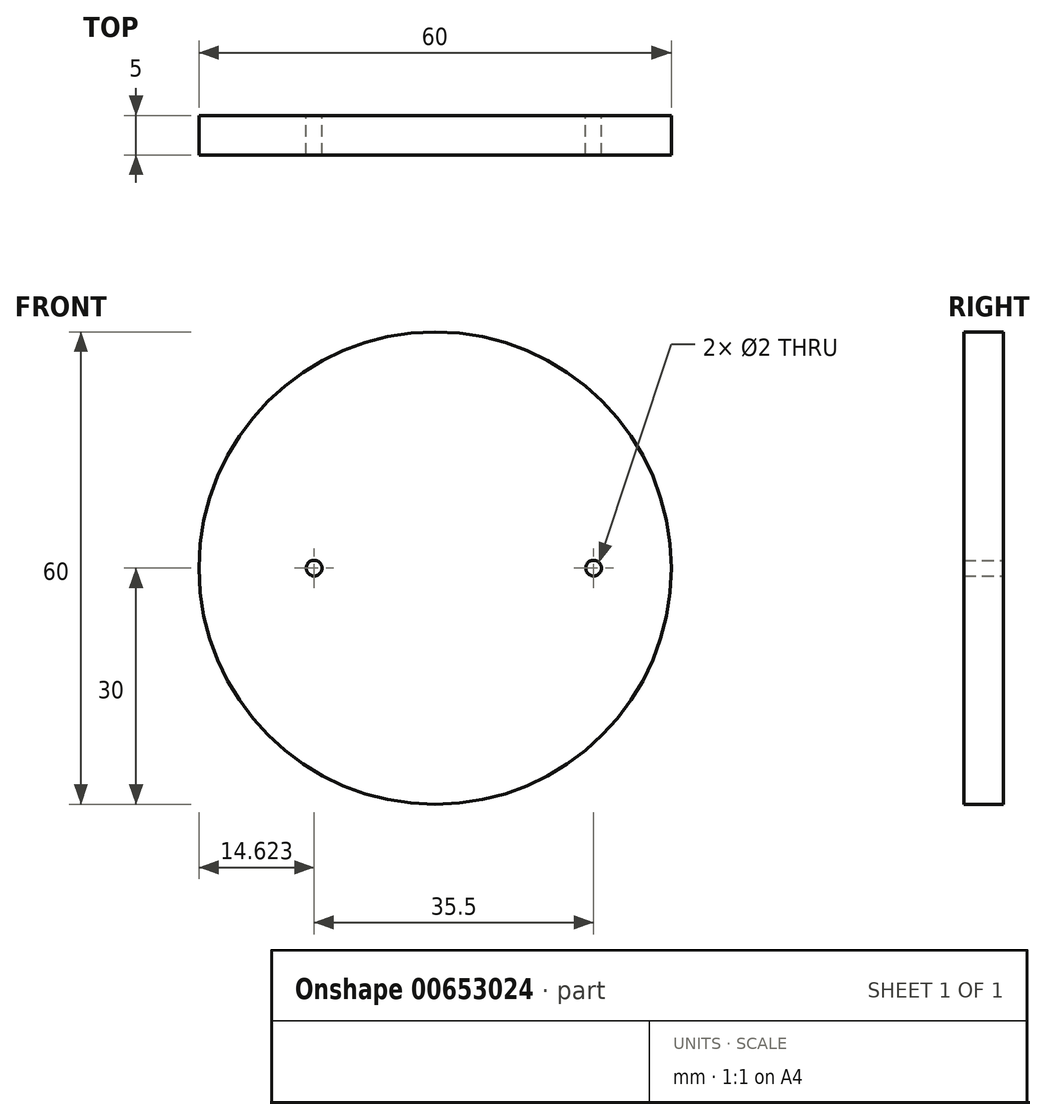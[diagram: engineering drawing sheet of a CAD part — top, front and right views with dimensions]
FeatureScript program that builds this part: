
annotation { "Feature Type Name" : "Feature", "Feature Type Description" : "" }
export const myFeature = defineFeature(function(context is Context, id is Id, definition is map)
    precondition{}
    {
        {
            var Q0;
            Q0=qCreatedBy(makeId("Front.planeOp"),FACE);
            var sketch = newSketch(context, id + "F0", { "sketchPlane" : qUnion([Q0])});
            skCircle(sketch, "E0", {"center": v(0, 0) * mm, "radius": 30 * mm});
            skCircle(sketch, "E1", {"center": v(20.12, 0) * mm, "radius": 1 * mm});
            skCircle(sketch, "E2", {"center": v(-15.38, 0) * mm, "radius": 1 * mm});
            skFitSpline(sketch, "E3", {"points": [v(-13.73, 18.62) * mm, v(-21.55, 16.33) * mm, v(-19.83, 10.31) * mm, v(-26.9, 5.93) * mm, v(-24.89, -0.94) * mm, v(-25.84, -10.2) * mm, v(-21.36, -10.3) * mm, v(-16.97, -17.07) * mm, v(-10.67, -16.78) * mm, v(-8.48, -23.56) * mm, v(1.73, -22.03) * mm, v(6.88, -25.08) * mm, v(8.7, -25.37) * mm, v(17.38, -16.4) * mm, v(19.67, -17.54) * mm, v(20.81, -14.68) * mm, v(21.67, -10.58) * mm, v(26.06, -9.34) * mm, v(23.67, -2.28) * mm, v(26.92, 4.2) * mm, v(23.58, 9.93) * mm, v(22.15, 17.37) * mm, v(11.94, 20.05) * mm, v(9.7, 25.39) * mm, v(2.91, 19.9) * mm, v(-6.8, 23.56) * mm, v(-13.77, 24.29) * mm, v(-13.73, 18.62) * mm]});
            skLineSegment(sketch, "E4", {"start": v(-4.64, -5.3) * mm, "end": v(0, 6.66) * mm});
            skLineSegment(sketch, "E5", {"start": v(0, 6.66) * mm, "end": v(5.35, -5.3) * mm});
            skLineSegment(sketch, "E6", {"start": v(5.35, -5.3) * mm, "end": v(-6.86, 1.85) * mm});
            skLineSegment(sketch, "E7", {"start": v(-6.86, 1.85) * mm, "end": v(6.7, 1.85) * mm});
            skLineSegment(sketch, "E8", {"start": v(6.7, 1.85) * mm, "end": v(-4.64, -5.3) * mm});
            skSolve(sketch);
        }
        {
            var Q0;
            Q0=makeQuery(id+"F0.imprint","IMPRINT",FACE,{"disambiguationData":[TD([[makeQuery(id+"F0.imprint","IMPRINT",EDGE,{"derivedFrom":sQuery(id+"F0.wireOp",EDGE,"E0")}),1.0]])]});
            var Q1;
            {var subQ1=sQuery(id+"F0.wireOp",EDGE,"E4");var subQ5=sQuery(id+"F0.wireOp",EDGE,"E6");var subQ6=makeQuery(id+"F0.imprint","INTERSECT",VERTEX,{"derivedFrom":[subQ1,subQ5]});Q1=makeQuery(id+"F0.imprint","IMPRINT",FACE,{"disambiguationData":[TD([[makeQuery(id+"F0.imprint","IMPRINT",EDGE,{"disambiguationData":[TD([[subQ6,-1.0]])],"derivedFrom":subQ1}),-1.0]])]});}
            var Q2;
            {var subQ0=sQuery(id+"F0.wireOp",EDGE,"E6");var subQ1=sQuery(id+"F0.wireOp",EDGE,"E5");var subQ2=makeQuery(id+"F0.imprint","INTERSECT",VERTEX,{"derivedFrom":[subQ1,subQ0]});Q2=makeQuery(id+"F0.imprint","IMPRINT",FACE,{"disambiguationData":[TD([[makeQuery(id+"F0.imprint","IMPRINT",EDGE,{"disambiguationData":[TD([[subQ2,1.0]])],"derivedFrom":subQ1}),-1.0]])]});}
            var Q3;
            {var subQ0=sQuery(id+"F0.wireOp",EDGE,"E8");var subQ1=sQuery(id+"F0.wireOp",EDGE,"E4");var subQ2=makeQuery(id+"F0.imprint","INTERSECT",VERTEX,{"derivedFrom":[subQ1,subQ0]});Q3=makeQuery(id+"F0.imprint","IMPRINT",FACE,{"disambiguationData":[TD([[makeQuery(id+"F0.imprint","IMPRINT",EDGE,{"disambiguationData":[TD([[subQ2,-1.0]])],"derivedFrom":subQ1}),-1.0]])]});}
            var Q4;
            {var subQ0=sQuery(id+"F0.wireOp",EDGE,"E6");var subQ1=sQuery(id+"F0.wireOp",EDGE,"E4");var subQ2=makeQuery(id+"F0.imprint","INTERSECT",VERTEX,{"derivedFrom":[subQ1,subQ0]});Q4=makeQuery(id+"F0.imprint","IMPRINT",FACE,{"disambiguationData":[TD([[makeQuery(id+"F0.imprint","IMPRINT",EDGE,{"disambiguationData":[TD([[subQ2,-1.0]])],"derivedFrom":subQ1}),1.0]])]});}
            var Q5;
            {var subQ0=sQuery(id+"F0.wireOp",EDGE,"E7");var subQ1=sQuery(id+"F0.wireOp",EDGE,"E5");var subQ2=makeQuery(id+"F0.imprint","INTERSECT",VERTEX,{"derivedFrom":[subQ1,subQ0]});Q5=makeQuery(id+"F0.imprint","IMPRINT",FACE,{"disambiguationData":[TD([[makeQuery(id+"F0.imprint","IMPRINT",EDGE,{"disambiguationData":[TD([[subQ2,-1.0]])],"derivedFrom":subQ1}),1.0]])]});}
            var Q6;
            Q6=makeQuery(id+"F0.imprint","IMPRINT",FACE,{"disambiguationData":[TD([[makeQuery(id+"F0.imprint","IMPRINT",EDGE,{"derivedFrom":sQuery(id+"F0.wireOp",EDGE,"E1")}),-1.0]])]});
            var Q7;
            {var subQ0=sQuery(id+"F0.wireOp",EDGE,"E5");var subQ1=sQuery(id+"F0.wireOp",EDGE,"E4");var subQ2=makeQuery(id+"F0.imprint","INTERSECT",VERTEX,{"derivedFrom":[subQ1,subQ0]});Q7=makeQuery(id+"F0.imprint","IMPRINT",FACE,{"disambiguationData":[TD([[makeQuery(id+"F0.imprint","IMPRINT",EDGE,{"disambiguationData":[TD([[subQ2,1.0]])],"derivedFrom":subQ1}),-1.0]])]});}
            extrude(context, id + "F1", {"entities" : qUnion([Q0, Q1, Q2, Q3, Q4, Q5, Q6, Q7]), "depth" : 5 * mm, "offsetDistance" : 25 * mm});
        }
    });
